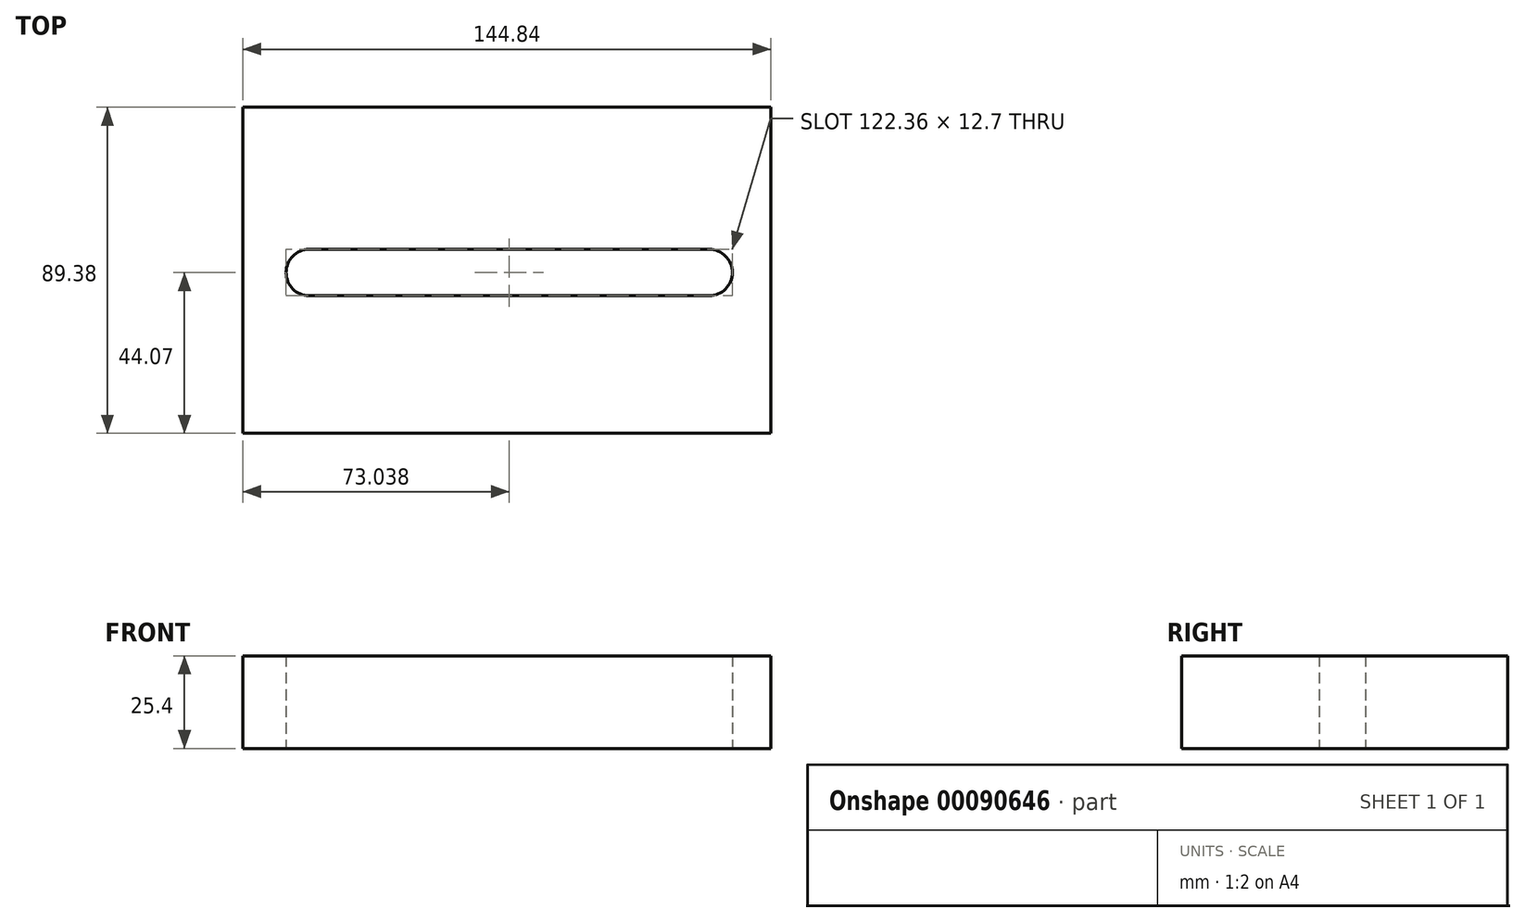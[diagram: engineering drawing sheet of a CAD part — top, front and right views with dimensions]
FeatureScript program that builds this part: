
annotation { "Feature Type Name" : "Feature", "Feature Type Description" : "" }
export const myFeature = defineFeature(function(context is Context, id is Id, definition is map)
    precondition{}
    {
        {
            var Q0;
            Q0=qCreatedBy(makeId("Top.planeOp"),FACE);
            var sketch = newSketch(context, id + "F0", { "sketchPlane" : qUnion([Q0])});
            skLineSegment(sketch, "E0.bottom", {"start": v(-83.6, 45.31) * mm, "end": v(61.25, 45.31) * mm});
            skLineSegment(sketch, "E0.top", {"start": v(-83.6, -44.07) * mm, "end": v(61.25, -44.07) * mm});
            skLineSegment(sketch, "E0.left", {"start": v(-83.6, 45.31) * mm, "end": v(-83.6, -44.07) * mm});
            skLineSegment(sketch, "E0.right", {"start": v(61.25, 45.31) * mm, "end": v(61.25, -44.07) * mm});
            skSolve(sketch);
        }
        {
            var Q0;
            Q0=qCreatedBy(makeId("Top.planeOp"),FACE);
            var sketch = newSketch(context, id + "F1", { "sketchPlane" : qUnion([Q0])});
            skLineSegment(sketch, "E1", {"start": v(-65.38, 0) * mm, "end": v(44.28, 0) * mm});
            skArc(sketch, "E2.0.startCap", {"start": v(-65.38, -6.35) * mm, "mid": v(-71.73, 0) * mm, "end": v(-65.38, 6.35) * mm});
            skArc(sketch, "E2.0.endCap", {"start": v(44.28, 6.35) * mm, "mid": v(50.63, 0) * mm, "end": v(44.28, -6.35) * mm});
            skLineSegment(sketch, "E2.0.left", {"start": v(-65.38, 6.35) * mm, "end": v(44.28, 6.35) * mm});
            skLineSegment(sketch, "E2.0.right", {"start": v(-65.38, -6.35) * mm, "end": v(44.28, -6.35) * mm});
            skSolve(sketch);
        }
        {
            var Q0;
            Q0=makeQuery(id+"F0.imprint","IMPRINT",FACE,{"disambiguationData":[TD([[makeQuery(id+"F0.imprint","IMPRINT",EDGE,{"derivedFrom":sQuery(id+"F0.wireOp",EDGE,"E0.bottom")}),-1.0]])]});
            extrude(context, id + "F2", {"entities" : qUnion([Q0]), "depth" : 25.4 * mm});
        }
        {
            var Q0;
            Q0 = qSketchRegion(id + "F1", true);
            extrude(context, id + "F3", {"entities" : qUnion([Q0]), "operationType" : NewBodyOperationType.REMOVE, "endBound" : BoundingType.THROUGH_ALL, "depth" : 25.4 * mm});
        }
    });
